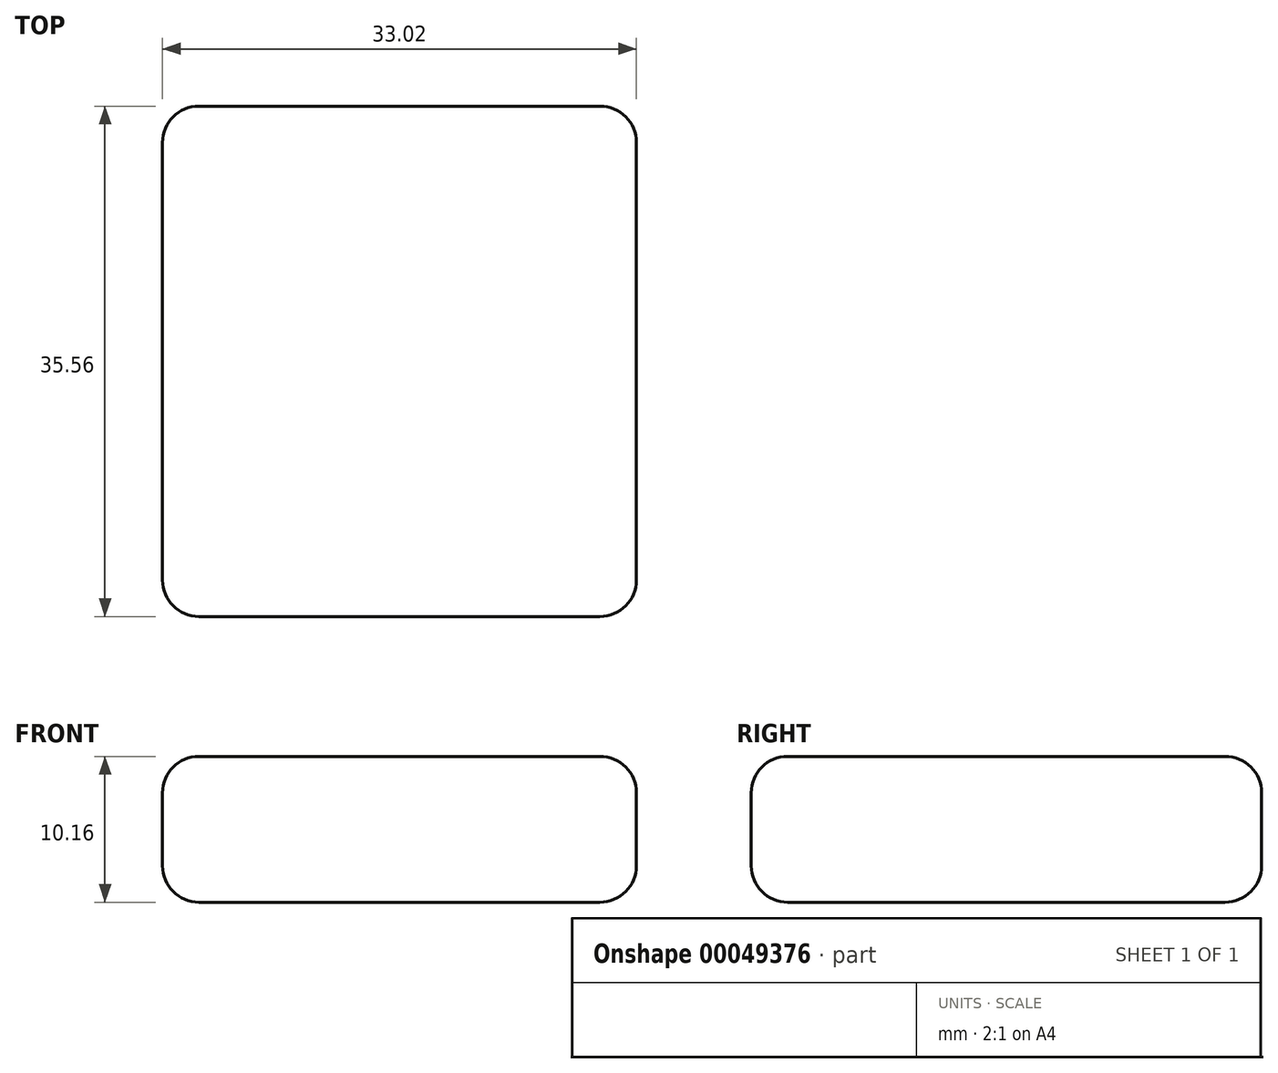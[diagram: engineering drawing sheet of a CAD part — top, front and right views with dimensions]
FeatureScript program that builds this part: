
annotation { "Feature Type Name" : "Feature", "Feature Type Description" : "" }
export const myFeature = defineFeature(function(context is Context, id is Id, definition is map)
    precondition{}
    {
        {
            var Q0;
            Q0=qCreatedBy(makeId("Top.planeOp"),FACE);
            var sketch = newSketch(context, id + "F0", { "sketchPlane" : qUnion([Q0])});
            skLineSegment(sketch, "E0.bottom", {"start": v(0, 0) * mm, "end": v(-33.02, 0) * mm});
            skLineSegment(sketch, "E0.top", {"start": v(0, -35.56) * mm, "end": v(-33.02, -35.56) * mm});
            skLineSegment(sketch, "E0.left", {"start": v(0, 0) * mm, "end": v(0, -35.56) * mm});
            skLineSegment(sketch, "E0.right", {"start": v(-33.02, 0) * mm, "end": v(-33.02, -35.56) * mm});
            skSolve(sketch);
        }
        {
            var Q0;
            Q0 = qSketchRegion(id + "F0", true);
            extrude(context, id + "F1", {"entities" : qUnion([Q0]), "depth" : 10.16 * mm});
        }
        {
            var Q0;
            Q0=makeQuery(id+"F1.opExtrude","CAP_FACE",FACE,{"disambiguationData":[OSD([sQuery(id+"F0.wireOp",EDGE,"E0.bottom"),sQuery(id+"F0.wireOp",EDGE,"E0.top"),sQuery(id+"F0.wireOp",EDGE,"E0.left"),sQuery(id+"F0.wireOp",EDGE,"E0.right")])],"isStart":false});
            var Q1;
            Q1=makeQuery(id+"F1.opExtrude","CAP_FACE",FACE,{"disambiguationData":[OSD([sQuery(id+"F0.wireOp",EDGE,"E0.bottom"),sQuery(id+"F0.wireOp",EDGE,"E0.top"),sQuery(id+"F0.wireOp",EDGE,"E0.left"),sQuery(id+"F0.wireOp",EDGE,"E0.right")])],"isStart":true});
            var Q2;
            Q2=makeQuery(id+"F1.opExtrude","SWEPT_FACE",FACE,{"disambiguationData":[OSD([sQuery(id+"F0.wireOp",EDGE,"E0.left")])]});
            var Q3;
            Q3=makeQuery(id+"F1.opExtrude","SWEPT_FACE",FACE,{"disambiguationData":[OSD([sQuery(id+"F0.wireOp",EDGE,"E0.right")])]});
            fillet(context, id + "F2", {"entities" : qUnion([Q0, Q1, Q2, Q3]), "radius" : 2.54 * mm, "tangentPropagation" : true, "allowEdgeOverflow" : false});
        }
    });
